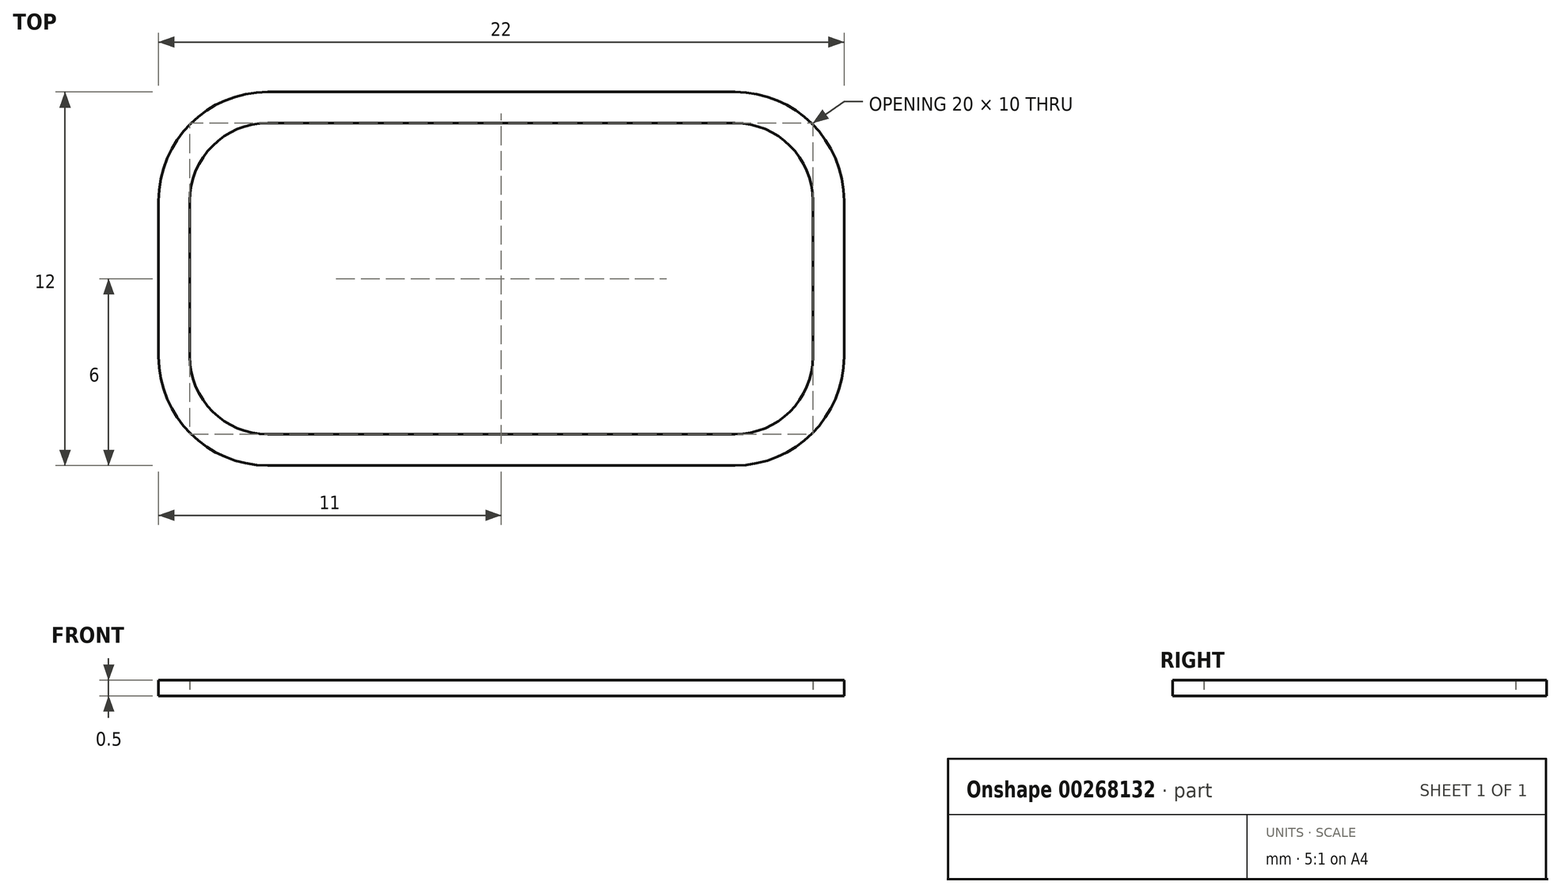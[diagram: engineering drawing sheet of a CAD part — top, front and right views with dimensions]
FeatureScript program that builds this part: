
annotation { "Feature Type Name" : "Feature", "Feature Type Description" : "" }
export const myFeature = defineFeature(function(context is Context, id is Id, definition is map)
    precondition{}
    {
        {
            var Q0;
            Q0=qCreatedBy(makeId("Top.planeOp"),FACE);
            var sketch = newSketch(context, id + "F0", { "sketchPlane" : qUnion([Q0])});
            skLineSegment(sketch, "E0.bottom", {"start": v(-7.5, 5) * mm, "end": v(7.5, 5) * mm});
            skLineSegment(sketch, "E0.top", {"start": v(-7.5, -5) * mm, "end": v(7.5, -5) * mm});
            skLineSegment(sketch, "E0.left", {"start": v(-10, 2.5) * mm, "end": v(-10, -2.5) * mm});
            skLineSegment(sketch, "E0.right", {"start": v(10, 2.5) * mm, "end": v(10, -2.5) * mm});
            skPoint(sketch, "E0.middle", {"position": v(0, 0) * mm});
            skPoint(sketch, "E1.visualSharp", {"position": v(-10, 5) * mm});
            skArc(sketch, "E1.filletArc", {"start": v(-7.5, 5) * mm, "mid": v(-9.27, 4.27) * mm, "end": v(-10, 2.5) * mm});
            skPoint(sketch, "E2.visualSharp", {"position": v(10, 5) * mm});
            skArc(sketch, "E2.filletArc", {"start": v(10, 2.5) * mm, "mid": v(9.27, 4.27) * mm, "end": v(7.5, 5) * mm});
            skPoint(sketch, "E3.visualSharp", {"position": v(10, -5) * mm});
            skArc(sketch, "E3.filletArc", {"start": v(7.5, -5) * mm, "mid": v(9.27, -4.27) * mm, "end": v(10, -2.5) * mm});
            skPoint(sketch, "E4.visualSharp", {"position": v(-10, -5) * mm});
            skArc(sketch, "E4.filletArc", {"start": v(-10, -2.5) * mm, "mid": v(-9.27, -4.27) * mm, "end": v(-7.5, -5) * mm});
            skLineSegment(sketch, "E5.bottom", {"start": v(-7.5, 6) * mm, "end": v(7.5, 6) * mm});
            skLineSegment(sketch, "E5.top", {"start": v(-7.5, -6) * mm, "end": v(7.5, -6) * mm});
            skLineSegment(sketch, "E5.left", {"start": v(-11, 2.5) * mm, "end": v(-11, -2.5) * mm});
            skLineSegment(sketch, "E5.right", {"start": v(11, 2.5) * mm, "end": v(11, -2.5) * mm});
            skPoint(sketch, "E6.visualSharp", {"position": v(-11, 6) * mm});
            skArc(sketch, "E6.filletArc", {"start": v(-7.5, 6) * mm, "mid": v(-9.97, 4.97) * mm, "end": v(-11, 2.5) * mm});
            skPoint(sketch, "E7.visualSharp", {"position": v(11, 6) * mm});
            skArc(sketch, "E7.filletArc", {"start": v(11, 2.5) * mm, "mid": v(9.97, 4.97) * mm, "end": v(7.5, 6) * mm});
            skPoint(sketch, "E8.visualSharp", {"position": v(11, -6) * mm});
            skArc(sketch, "E8.filletArc", {"start": v(7.5, -6) * mm, "mid": v(9.97, -4.97) * mm, "end": v(11, -2.5) * mm});
            skPoint(sketch, "E9.visualSharp", {"position": v(-11, -6) * mm});
            skArc(sketch, "E9.filletArc", {"start": v(-11, -2.5) * mm, "mid": v(-9.97, -4.97) * mm, "end": v(-7.5, -6) * mm});
            skSolve(sketch);
        }
        {
            var Q0;
            Q0=makeQuery(id+"F0.imprint","IMPRINT",FACE,{"disambiguationData":[TD([[makeQuery(id+"F0.imprint","IMPRINT",EDGE,{"derivedFrom":sQuery(id+"F0.wireOp",EDGE,"E0.bottom")}),1.0]])]});
            extrude(context, id + "F1", {"entities" : qUnion([Q0]), "depth" : 0.5 * mm, "offsetDistance" : 25 * mm});
        }
    });
